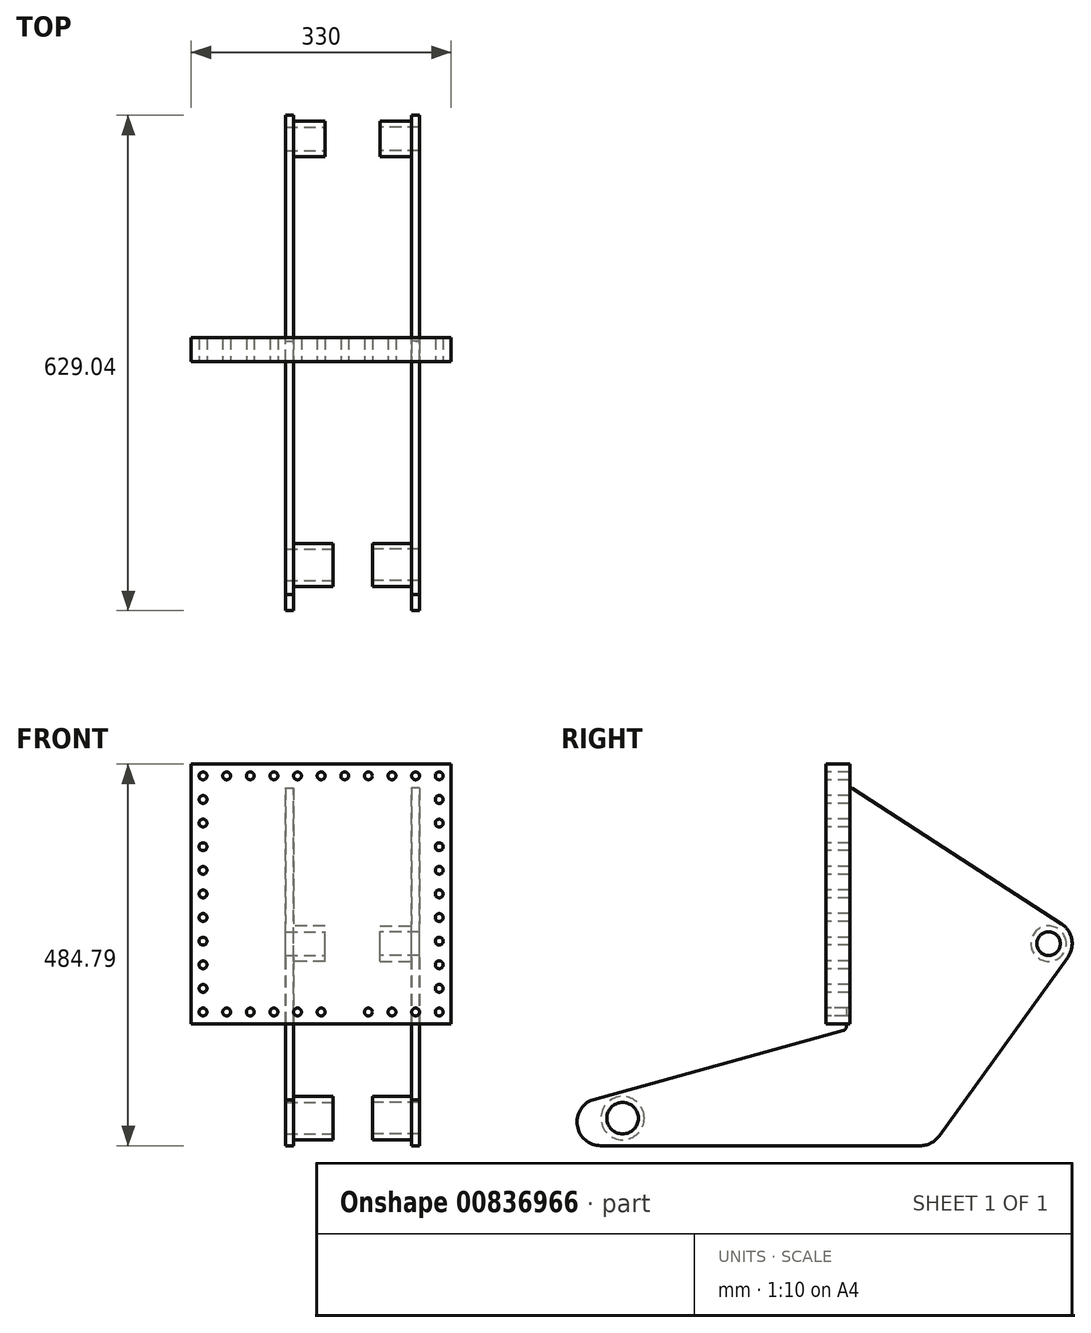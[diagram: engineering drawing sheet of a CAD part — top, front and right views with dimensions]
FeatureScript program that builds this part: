
annotation { "Feature Type Name" : "Feature", "Feature Type Description" : "" }
export const myFeature = defineFeature(function(context is Context, id is Id, definition is map)
    precondition{}
    {
        {
            var Q0;
            Q0=qCreatedBy(makeId("Front.planeOp"),FACE);
            var sketch = newSketch(context, id + "F0", { "sketchPlane" : qUnion([Q0])});
            skLineSegment(sketch, "E0.0", {"start": v(150, 150) * mm, "end": v(150, -165) * mm, "construction": true});
            skLineSegment(sketch, "E0.1", {"start": v(-135, -351.73) * mm, "end": v(-135, -141.33) * mm});
            skLineSegment(sketch, "E0.2", {"start": v(75, -351.73) * mm, "end": v(75, -141.33) * mm});
            skLineSegment(sketch, "E0.3", {"start": v(185, -185) * mm, "end": v(-185, -185) * mm});
            skLineSegment(sketch, "E0.7", {"start": v(165, 165) * mm, "end": v(165, -165) * mm});
            skLineSegment(sketch, "E0.8", {"start": v(135, 135) * mm, "end": v(135, -135) * mm});
            skLineSegment(sketch, "E0.9", {"start": v(165, -165) * mm, "end": v(-165, -165) * mm});
            skLineSegment(sketch, "E0.10", {"start": v(165, 165) * mm, "end": v(-165, 165) * mm});
            skLineSegment(sketch, "E0.11", {"start": v(-165, 165) * mm, "end": v(-165, -165) * mm});
            skLineSegment(sketch, "E0.13", {"start": v(135, -135) * mm, "end": v(-135, -135) * mm});
            skLineSegment(sketch, "E0.14", {"start": v(135, 135) * mm, "end": v(-135, 135) * mm});
            skLineSegment(sketch, "E0.15", {"start": v(-135, 135) * mm, "end": v(-135, -135) * mm});
            skCircle(sketch, "E0.18", {"center": v(-30, -285) * mm, "radius": 60 * mm});
            skCircle(sketch, "E0.21", {"center": v(30, -150) * mm, "radius": 5 * mm});
            skCircle(sketch, "E0.22", {"center": v(150, -120) * mm, "radius": 5 * mm});
            skCircle(sketch, "E0.23", {"center": v(-150, 30) * mm, "radius": 5 * mm});
            skCircle(sketch, "E0.24", {"center": v(-120, -150) * mm, "radius": 5 * mm});
            skCircle(sketch, "E0.25", {"center": v(-120, 150) * mm, "radius": 5 * mm});
            skCircle(sketch, "E0.26", {"center": v(-150, 60) * mm, "radius": 5 * mm});
            skLineSegment(sketch, "E0.27", {"start": v(150, 150) * mm, "end": v(150, 120) * mm});
            skCircle(sketch, "E0.28", {"center": v(-60, -150) * mm, "radius": 5 * mm});
            skLineSegment(sketch, "E0.29", {"start": v(-135, -351.73) * mm, "end": v(-135, -185) * mm});
            skCircle(sketch, "E0.30", {"center": v(-30, -285) * mm, "radius": 60 * mm});
            skCircle(sketch, "E0.31", {"center": v(120, -150) * mm, "radius": 5 * mm});
            skCircle(sketch, "E0.32", {"center": v(60, 150) * mm, "radius": 5 * mm});
            skCircle(sketch, "E0.33", {"center": v(150, -30) * mm, "radius": 5 * mm});
            skCircle(sketch, "E0.34", {"center": v(-150, -30) * mm, "radius": 5 * mm});
            skCircle(sketch, "E0.35", {"center": v(-150, 90) * mm, "radius": 5 * mm});
            skCircle(sketch, "E0.36", {"center": v(150, 90) * mm, "radius": 5 * mm});
            skCircle(sketch, "E0.38", {"center": v(90, -150) * mm, "radius": 5 * mm});
            skCircle(sketch, "E0.39", {"center": v(30, 150) * mm, "radius": 5 * mm});
            skCircle(sketch, "E0.40", {"center": v(150, -60) * mm, "radius": 5 * mm});
            skCircle(sketch, "E0.41", {"center": v(-150, 0) * mm, "radius": 5 * mm});
            skCircle(sketch, "E0.42", {"center": v(-90, -150) * mm, "radius": 5 * mm});
            skLineSegment(sketch, "E0.43", {"start": v(165, 165) * mm, "end": v(165, -165) * mm});
            skCircle(sketch, "E0.46", {"center": v(150, -150) * mm, "radius": 5 * mm});
            skLineSegment(sketch, "E0.47", {"start": v(135, 135) * mm, "end": v(135, -135) * mm});
            skCircle(sketch, "E0.49", {"center": v(150, -90) * mm, "radius": 5 * mm});
            skCircle(sketch, "E0.50", {"center": v(60, -150) * mm, "radius": 5 * mm});
            skCircle(sketch, "E0.51", {"center": v(90, 150) * mm, "radius": 5 * mm});
            skCircle(sketch, "E0.52", {"center": v(-150, -60) * mm, "radius": 5 * mm});
            skCircle(sketch, "E0.53", {"center": v(120, 150) * mm, "radius": 5 * mm});
            skCircle(sketch, "E0.54", {"center": v(150, 0) * mm, "radius": 5 * mm});
            skCircle(sketch, "E0.55", {"center": v(-150, -90) * mm, "radius": 5 * mm});
            skCircle(sketch, "E0.56", {"center": v(-60, 150) * mm, "radius": 5 * mm});
            skCircle(sketch, "E0.57", {"center": v(-150, -120) * mm, "radius": 5 * mm});
            skCircle(sketch, "E0.58", {"center": v(-90, 150) * mm, "radius": 5 * mm});
            skCircle(sketch, "E0.59", {"center": v(150, 60) * mm, "radius": 5 * mm});
            skCircle(sketch, "E0.60", {"center": v(-150, 150) * mm, "radius": 5 * mm});
            skCircle(sketch, "E0.61", {"center": v(150, 120) * mm, "radius": 5 * mm});
            skCircle(sketch, "E0.62", {"center": v(-30, -150) * mm, "radius": 5 * mm});
            skCircle(sketch, "E0.63", {"center": v(-150, 120) * mm, "radius": 5 * mm});
            skCircle(sketch, "E0.64", {"center": v(150, 30) * mm, "radius": 5 * mm});
            skCircle(sketch, "E0.65", {"center": v(-150, -150) * mm, "radius": 5 * mm});
            skCircle(sketch, "E0.66", {"center": v(-150, -150) * mm, "radius": 5 * mm});
            skCircle(sketch, "E0.67", {"center": v(0, 150) * mm, "radius": 5 * mm});
            skCircle(sketch, "E0.68", {"center": v(150, 30) * mm, "radius": 5 * mm});
            skCircle(sketch, "E0.69", {"center": v(-30, 150) * mm, "radius": 5 * mm});
            skCircle(sketch, "E0.70", {"center": v(150, 150) * mm, "radius": 5 * mm});
            skCircle(sketch, "E0.71", {"center": v(0, -150) * mm, "radius": 5 * mm});
            skCircle(sketch, "E0.72", {"center": v(150, 150) * mm, "radius": 5 * mm});
            skSolve(sketch);
        }
        {
            var Q0;
            Q0=makeQuery(id+"F0.imprint","IMPRINT",FACE,{"disambiguationData":[TD([[makeQuery(id+"F0.imprint","IMPRINT",EDGE,{"derivedFrom":sQuery(id+"F0.wireOp",EDGE,"E0.10")}),1.0]])]});
            var Q1;
            Q1=makeQuery(id+"F0.imprint","IMPRINT",FACE,{"disambiguationData":[TD([[makeQuery(id+"F0.imprint","IMPRINT",EDGE,{"derivedFrom":sQuery(id+"F0.wireOp",EDGE,"E0.21")}),1.0]])]});
            var Q2;
            Q2=makeQuery(id+"F0.imprint","IMPRINT",FACE,{"disambiguationData":[TD([[makeQuery(id+"F0.imprint","IMPRINT",EDGE,{"derivedFrom":sQuery(id+"F0.wireOp",EDGE,"E0.13")}),-1.0]])]});
            extrude(context, id + "F1", {"entities" : qUnion([Q0, Q1, Q2]), "oppositeDirection" : true, "depth" : 30 * mm, "offsetDistance" : 25 * mm});
        }
        {
            var Q0;
            Q0=qCreatedBy(makeId("Right.planeOp"),FACE);
            var sketch = newSketch(context, id + "F2", { "sketchPlane" : qUnion([Q0])});
            skLineSegment(sketch, "E1", {"start": v(33.35, 134.13) * mm, "end": v(298.89, -37.98) * mm});
            skLineSegment(sketch, "E2", {"start": v(306.92, -80.68) * mm, "end": v(143.74, -307.32) * mm});
            skLineSegment(sketch, "E3", {"start": v(119.4, -319.8) * mm, "end": v(-286.47, -319.8) * mm});
            skPoint(sketch, "E4.visualSharp", {"position": v(325.33, -55.12) * mm});
            skArc(sketch, "E4.filletArc", {"start": v(306.92, -80.68) * mm, "mid": v(312.05, -57.61) * mm, "end": v(298.89, -37.98) * mm});
            skPoint(sketch, "E5.visualSharp", {"position": v(134.76, -319.8) * mm});
            skArc(sketch, "E5.filletArc", {"start": v(119.4, -319.8) * mm, "mid": v(133.07, -316.5) * mm, "end": v(143.74, -307.32) * mm});
            skPoint(sketch, "E6.visualSharp", {"position": v(-405.49, -319.8) * mm});
            skArc(sketch, "E6.filletArc", {"start": v(-296.28, -261.44) * mm, "mid": v(-316.06, -294.76) * mm, "end": v(-286.47, -319.8) * mm});
            skLineSegment(sketch, "E7", {"start": v(25.63, 129.93) * mm, "end": v(25.63, -168.74) * mm});
            skLineSegment(sketch, "E8", {"start": v(-296.28, -261.44) * mm, "end": v(21.96, -173.56) * mm});
            skCircle(sketch, "E9", {"center": v(282.57, -63.15) * mm, "radius": 15 * mm});
            skCircle(sketch, "E10", {"center": v(-258.52, -284.83) * mm, "radius": 20 * mm});
            skPoint(sketch, "E11.visualSharp", {"position": v(25.63, -172.55) * mm});
            skArc(sketch, "E11.filletArc", {"start": v(21.96, -173.56) * mm, "mid": v(24.6, -171.77) * mm, "end": v(25.63, -168.74) * mm});
            skPoint(sketch, "E12.visualSharp", {"position": v(25.63, 139.13) * mm});
            skArc(sketch, "E12.filletArc", {"start": v(33.35, 134.13) * mm, "mid": v(28.24, 134.33) * mm, "end": v(25.63, 129.93) * mm});
            skSolve(sketch);
        }
        {
            var Q0;
            Q0=makeQuery(id+"F2.imprint","IMPRINT",FACE,{"disambiguationData":[TD([[makeQuery(id+"F2.imprint","IMPRINT",EDGE,{"derivedFrom":sQuery(id+"F2.wireOp",EDGE,"E1")}),-1.0]])]});
            cPlane(context, id + "F3", {"entities" : qUnion([Q0]), "cplaneType" : CPlaneType.OFFSET, "offset" : 115 * mm, "width" : 150 * mm, "height" : 150 * mm});
        }
        {
            var Q0;
            Q0=qCreatedBy(id+"F3.planeOp",FACE);
            var sketch = newSketch(context, id + "F4", { "sketchPlane" : qUnion([Q0])});
            skLineSegment(sketch, "E13.0", {"start": v(33.35, 134.13) * mm, "end": v(298.89, -37.98) * mm});
            skArc(sketch, "E14.0", {"start": v(306.92, -80.68) * mm, "mid": v(312.05, -57.61) * mm, "end": v(298.89, -37.98) * mm});
            skCircle(sketch, "E15.0", {"center": v(282.57, -63.15) * mm, "radius": 15 * mm});
            skLineSegment(sketch, "E16.0", {"start": v(306.92, -80.68) * mm, "end": v(143.74, -307.32) * mm});
            skArc(sketch, "E17.0", {"start": v(119.4, -319.8) * mm, "mid": v(133.07, -316.5) * mm, "end": v(143.74, -307.32) * mm});
            skLineSegment(sketch, "E18.0", {"start": v(119.4, -319.8) * mm, "end": v(-286.47, -319.8) * mm});
            skArc(sketch, "E19.0", {"start": v(-296.28, -261.44) * mm, "mid": v(-316.06, -294.76) * mm, "end": v(-286.47, -319.8) * mm});
            skLineSegment(sketch, "E20.0", {"start": v(-296.28, -261.44) * mm, "end": v(21.96, -173.56) * mm});
            skCircle(sketch, "E21.0", {"center": v(-258.52, -284.83) * mm, "radius": 20 * mm});
            skLineSegment(sketch, "E22.0", {"start": v(25.63, 129.93) * mm, "end": v(25.63, -168.74) * mm});
            skArc(sketch, "E23.0", {"start": v(33.35, 134.13) * mm, "mid": v(28.24, 134.33) * mm, "end": v(25.63, 129.93) * mm});
            skArc(sketch, "E24.0", {"start": v(21.96, -173.56) * mm, "mid": v(24.6, -171.77) * mm, "end": v(25.63, -168.74) * mm});
            skCircle(sketch, "E25", {"center": v(282.57, -63.15) * mm, "radius": 22.5 * mm});
            skSolve(sketch);
        }
        {
            var Q0;
            Q0=makeQuery(id+"F4.imprint","IMPRINT",FACE,{"disambiguationData":[TD([[makeQuery(id+"F4.imprint","IMPRINT",EDGE,{"derivedFrom":sQuery(id+"F4.wireOp",EDGE,"E13.0")}),-1.0]])]});
            var Q1;
            Q1=makeQuery(id+"F4.imprint","IMPRINT",FACE,{"disambiguationData":[TD([[makeQuery(id+"F4.imprint","IMPRINT",EDGE,{"derivedFrom":sQuery(id+"F4.wireOp",EDGE,"E15.0")}),-1.0]])]});
            extrude(context, id + "F5", {"entities" : qUnion([Q0, Q1]), "operationType" : NewBodyOperationType.ADD, "depth" : 10 * mm, "offsetDistance" : 25 * mm});
        }
        {
            var Q0;
            Q0=qCreatedBy(makeId("Right.planeOp"),FACE);
            cPlane(context, id + "F6", {"entities" : qUnion([Q0]), "cplaneType" : CPlaneType.OFFSET, "offset" : 35 * mm, "oppositeDirection" : true, "width" : 150 * mm, "height" : 150 * mm});
        }
        {
            var Q0;
            Q0=qCreatedBy(id+"F6.planeOp",FACE);
            var sketch = newSketch(context, id + "F7", { "sketchPlane" : qUnion([Q0])});
            skLineSegment(sketch, "E26.0", {"start": v(25.63, 129.93) * mm, "end": v(25.63, -168.74) * mm});
            skLineSegment(sketch, "E27.0", {"start": v(33.35, 134.13) * mm, "end": v(298.89, -37.98) * mm});
            skArc(sketch, "E28.0", {"start": v(33.35, 134.13) * mm, "mid": v(28.24, 134.33) * mm, "end": v(25.63, 129.93) * mm});
            skCircle(sketch, "E29.0", {"center": v(282.57, -63.15) * mm, "radius": 15 * mm});
            skArc(sketch, "E30.0", {"start": v(306.92, -80.68) * mm, "mid": v(312.05, -57.61) * mm, "end": v(298.89, -37.98) * mm});
            skPoint(sketch, "E31.0", {"position": v(225.33, -194) * mm});
            skLineSegment(sketch, "E32.0", {"start": v(306.92, -80.68) * mm, "end": v(143.74, -307.32) * mm});
            skArc(sketch, "E33.0", {"start": v(119.4, -319.8) * mm, "mid": v(133.07, -316.5) * mm, "end": v(143.74, -307.32) * mm});
            skLineSegment(sketch, "E34.0", {"start": v(119.4, -319.8) * mm, "end": v(-286.47, -319.8) * mm});
            skArc(sketch, "E35.0", {"start": v(-296.28, -261.44) * mm, "mid": v(-316.06, -294.76) * mm, "end": v(-286.47, -319.8) * mm});
            skLineSegment(sketch, "E36.0", {"start": v(-296.28, -261.44) * mm, "end": v(21.96, -173.56) * mm});
            skCircle(sketch, "E37.0", {"center": v(-258.52, -284.83) * mm, "radius": 20 * mm});
            skArc(sketch, "E38.0", {"start": v(21.96, -173.56) * mm, "mid": v(24.6, -171.77) * mm, "end": v(25.63, -168.74) * mm});
            skCircle(sketch, "E39", {"center": v(282.57, -63.15) * mm, "radius": 22.5 * mm});
            skSolve(sketch);
        }
        {
            var Q0;
            Q0=makeQuery(id+"F7.imprint","IMPRINT",FACE,{"disambiguationData":[TD([[makeQuery(id+"F7.imprint","IMPRINT",EDGE,{"derivedFrom":sQuery(id+"F7.wireOp",EDGE,"E26.0")}),1.0]])]});
            var Q1;
            Q1=makeQuery(id+"F7.imprint","IMPRINT",FACE,{"disambiguationData":[TD([[makeQuery(id+"F7.imprint","IMPRINT",EDGE,{"derivedFrom":sQuery(id+"F7.wireOp",EDGE,"E29.0")}),-1.0]])]});
            extrude(context, id + "F8", {"entities" : qUnion([Q0, Q1]), "operationType" : NewBodyOperationType.ADD, "oppositeDirection" : true, "depth" : 10 * mm, "offsetDistance" : 25 * mm});
        }
        {
            var Q0;
            Q0=makeQuery(id+"F7.imprint","IMPRINT",FACE,{"disambiguationData":[TD([[makeQuery(id+"F7.imprint","IMPRINT",EDGE,{"derivedFrom":sQuery(id+"F7.wireOp",EDGE,"E29.0")}),-1.0]])]});
            extrude(context, id + "F9", {"entities" : qUnion([Q0]), "operationType" : NewBodyOperationType.ADD, "depth" : 40 * mm, "offsetDistance" : 25 * mm});
        }
        {
            var Q0;
            Q0=makeQuery(id+"F4.imprint","IMPRINT",FACE,{"disambiguationData":[TD([[makeQuery(id+"F4.imprint","IMPRINT",EDGE,{"derivedFrom":sQuery(id+"F4.wireOp",EDGE,"E15.0")}),-1.0]])]});
            extrude(context, id + "F10", {"entities" : qUnion([Q0]), "operationType" : NewBodyOperationType.ADD, "oppositeDirection" : true, "depth" : 40 * mm, "offsetDistance" : 25 * mm});
        }
        {
            var Q0;
            Q0=makeQuery(id+"F4.imprint","IMPRINT",FACE,{"disambiguationData":[TD([[makeQuery(id+"F4.imprint","IMPRINT",EDGE,{"derivedFrom":sQuery(id+"F4.wireOp",EDGE,"E13.0")}),-1.0]])]});
            cPlane(context, id + "F11", {"entities" : qUnion([Q0]), "cplaneType" : CPlaneType.OFFSET, "offset" : 75 * mm, "oppositeDirection" : true, "width" : 150 * mm, "height" : 150 * mm});
        }
        {
            var Q0;
            Q0=qCreatedBy(id+"F11.planeOp",FACE);
            var sketch = newSketch(context, id + "F12", { "sketchPlane" : qUnion([Q0])});
            skCircle(sketch, "E40.0", {"center": v(-258.52, -284.83) * mm, "radius": 20 * mm});
            skSolve(sketch);
        }
        {
            var Q0;
            Q0=makeQuery(id+"F7.imprint","IMPRINT",FACE,{"disambiguationData":[TD([[makeQuery(id+"F7.imprint","IMPRINT",EDGE,{"derivedFrom":sQuery(id+"F7.wireOp",EDGE,"E26.0")}),1.0]])]});
            var sketch = newSketch(context, id + "F13", { "sketchPlane" : qUnion([Q0])});
            skCircle(sketch, "E41.0", {"center": v(-258.52, -284.83) * mm, "radius": 20 * mm});
            skCircle(sketch, "E42", {"center": v(-258.52, -284.83) * mm, "radius": 27.5 * mm});
            skSolve(sketch);
        }
        {
            var Q0;
            Q0=makeQuery(id+"F13.imprint","IMPRINT",FACE,{"disambiguationData":[TD([[makeQuery(id+"F13.imprint","IMPRINT",EDGE,{"derivedFrom":sQuery(id+"F13.wireOp",EDGE,"E41.0")}),-1.0]])]});
            extrude(context, id + "F14", {"entities" : qUnion([Q0]), "operationType" : NewBodyOperationType.ADD, "depth" : 50 * mm, "offsetDistance" : 25 * mm});
        }
        {
            var Q0;
            Q0=makeQuery(id+"F4.imprint","IMPRINT",FACE,{"disambiguationData":[TD([[makeQuery(id+"F4.imprint","IMPRINT",EDGE,{"derivedFrom":sQuery(id+"F4.wireOp",EDGE,"E13.0")}),-1.0]])]});
            var sketch = newSketch(context, id + "F15", { "sketchPlane" : qUnion([Q0])});
            skCircle(sketch, "E43.0", {"center": v(-258.52, -284.83) * mm, "radius": 20 * mm});
            skCircle(sketch, "E44", {"center": v(-258.52, -284.83) * mm, "radius": 27.5 * mm});
            skSolve(sketch);
        }
        {
            var Q0;
            Q0=makeQuery(id+"F15.imprint","IMPRINT",FACE,{"disambiguationData":[TD([[makeQuery(id+"F15.imprint","IMPRINT",EDGE,{"derivedFrom":sQuery(id+"F15.wireOp",EDGE,"E43.0")}),-1.0]])]});
            extrude(context, id + "F16", {"entities" : qUnion([Q0]), "operationType" : NewBodyOperationType.ADD, "oppositeDirection" : true, "depth" : 50 * mm, "offsetDistance" : 25 * mm});
        }
    });
